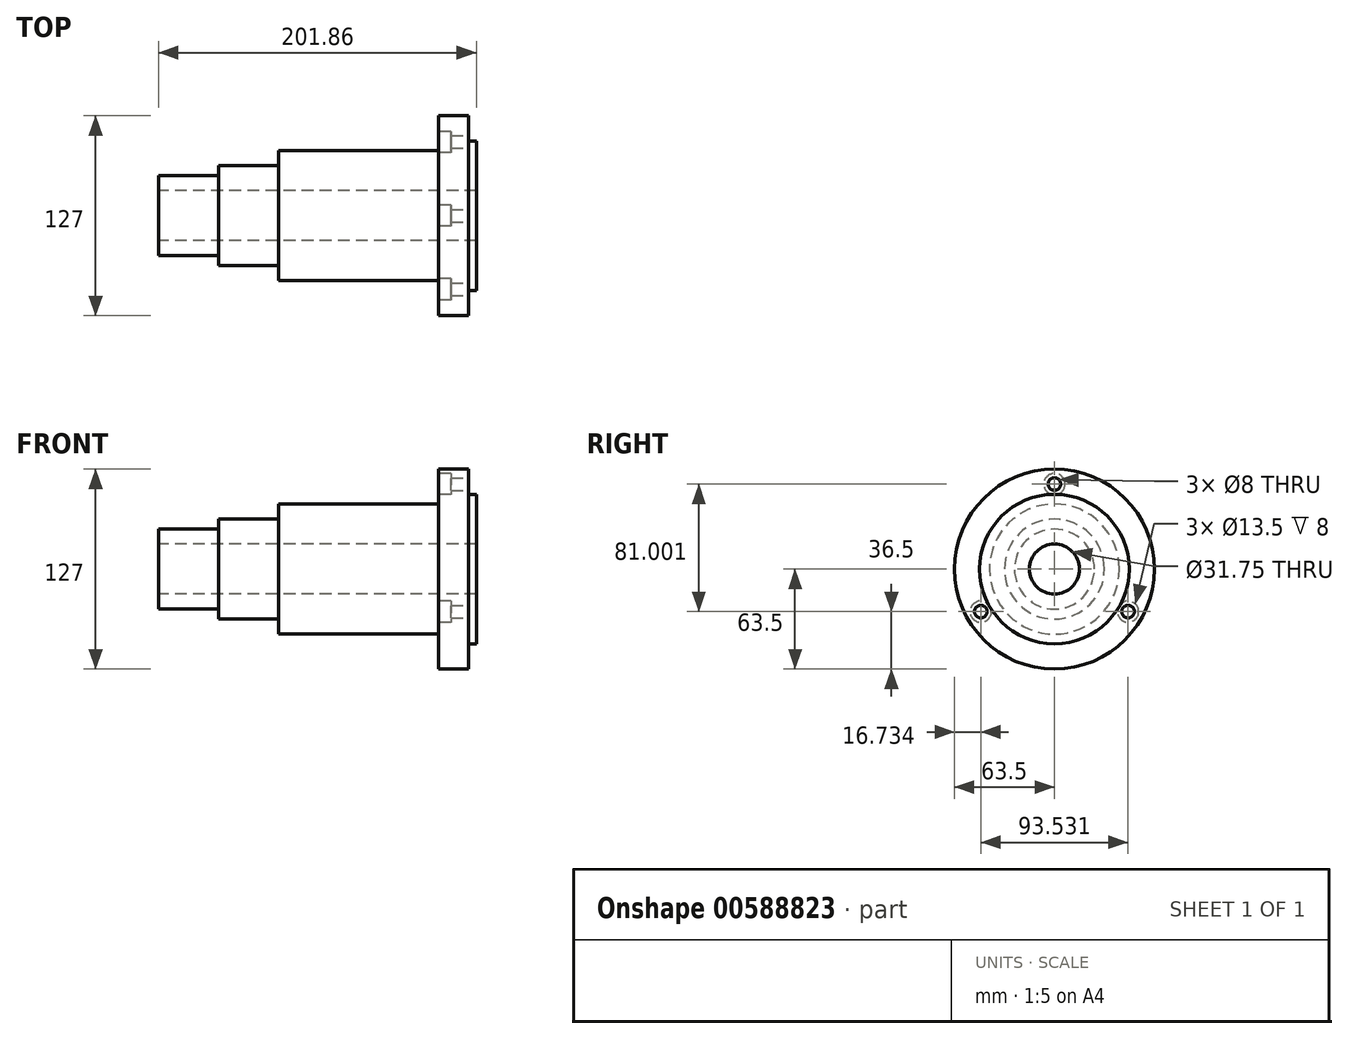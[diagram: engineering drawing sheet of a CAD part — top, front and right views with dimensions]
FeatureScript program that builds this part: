
annotation { "Feature Type Name" : "Feature", "Feature Type Description" : "" }
export const myFeature = defineFeature(function(context is Context, id is Id, definition is map)
    precondition{}
    {
        {
            var Q0;
            Q0=qCreatedBy(makeId("Front.planeOp"),FACE);
            var sketch = newSketch(context, id + "F0", { "sketchPlane" : qUnion([Q0])});
            skLineSegment(sketch, "E0", {"start": v(10.11, 15.88) * mm, "end": v(130.76, 15.88) * mm});
            skLineSegment(sketch, "E1", {"start": v(130.76, 47.5) * mm, "end": v(130.76, 63.5) * mm});
            skLineSegment(sketch, "E2", {"start": v(130.76, 63.5) * mm, "end": v(111.71, 63.5) * mm});
            skLineSegment(sketch, "E3", {"start": v(111.71, 63.5) * mm, "end": v(111.71, 41.28) * mm});
            skLineSegment(sketch, "E4", {"start": v(111.71, 41.28) * mm, "end": v(10.11, 41.28) * mm});
            skLineSegment(sketch, "E5", {"start": v(10.11, 41.28) * mm, "end": v(10.11, 31.75) * mm});
            skLineSegment(sketch, "E6.bottom", {"start": v(135.77, 47.5) * mm, "end": v(130.76, 47.5) * mm});
            skLineSegment(sketch, "E6.top", {"start": v(135.77, 15.88) * mm, "end": v(130.76, 15.88) * mm});
            skLineSegment(sketch, "E6.left", {"start": v(135.77, 47.5) * mm, "end": v(135.77, 15.88) * mm});
            skLineSegment(sketch, "E7.bottom", {"start": v(10.11, 15.88) * mm, "end": v(-47.18, 15.87) * mm});
            skLineSegment(sketch, "E7.top", {"start": v(10.11, 31.75) * mm, "end": v(-27.99, 31.75) * mm});
            skLineSegment(sketch, "E8.bottom", {"start": v(-47.18, 15.87) * mm, "end": v(-66.09, 15.87) * mm});
            skLineSegment(sketch, "E8.top", {"start": v(-27.99, 25.4) * mm, "end": v(-66.09, 25.4) * mm});
            skLineSegment(sketch, "E8.right", {"start": v(-66.09, 15.87) * mm, "end": v(-66.09, 25.4) * mm});
            skLineSegment(sketch, "E9", {"start": v(-27.99, 25.4) * mm, "end": v(-27.99, 31.75) * mm});
            skLineSegment(sketch, "E10", {"start": v(-72.6, 0) * mm, "end": v(74.38, 0) * mm});
            skSolve(sketch);
        }
        {
            var Q0;
            Q0=makeQuery(id+"F0.imprint","IMPRINT",FACE,{"disambiguationData":[TD([[makeQuery(id+"F0.imprint","IMPRINT",EDGE,{"derivedFrom":sQuery(id+"F0.wireOp",EDGE,"E0")}),1.0]])]});
            var Q1;
            Q1=sQuery(id+"F0.wireOp",EDGE,"E10");
            revolve(context, id + "F1", {"entities" : qUnion([Q0]), "axis" : qUnion([Q1]), "revolveType" : RevolveType.FULL});
        }
        {
            var Q0;
            Q0=makeQuery(id+"F1.opRevolve","SWEPT_FACE",FACE,{"disambiguationData":[OSD([sQuery(id+"F0.wireOp",EDGE,"E1")])]});
            var sketch = newSketch(context, id + "F2", { "sketchPlane" : qUnion([Q0])});
            skCircle(sketch, "E11", {"center": v(0, 0) * mm, "radius": 54 * mm, "construction": true});
            skCircle(sketch, "E12", {"center": v(0, 54) * mm, "radius": 4 * mm});
            skCircle(sketch, "E13.1.0", {"center": v(-46.77, -27) * mm, "radius": 4 * mm});
            skCircle(sketch, "E13.2.0", {"center": v(46.77, -27) * mm, "radius": 4 * mm});
            skSolve(sketch);
        }
        {
            var Q0;
            Q0=makeQuery(id+"F2.imprint","IMPRINT",FACE,{"disambiguationData":[TD([[makeQuery(id+"F2.imprint","IMPRINT",EDGE,{"derivedFrom":sQuery(id+"F2.wireOp",EDGE,"E12")}),1.0]])]});
            var Q1;
            Q1=makeQuery(id+"F2.imprint","IMPRINT",FACE,{"disambiguationData":[TD([[makeQuery(id+"F2.imprint","IMPRINT",EDGE,{"derivedFrom":sQuery(id+"F2.wireOp",EDGE,"E13.2.0")}),1.0]])]});
            var Q2;
            Q2=makeQuery(id+"F2.imprint","IMPRINT",FACE,{"disambiguationData":[TD([[makeQuery(id+"F2.imprint","IMPRINT",EDGE,{"derivedFrom":sQuery(id+"F2.wireOp",EDGE,"E13.1.0")}),1.0]])]});
            extrude(context, id + "F3", {"entities" : qUnion([Q0, Q1, Q2]), "operationType" : NewBodyOperationType.REMOVE, "oppositeDirection" : true, "depth" : 25.4 * mm, "offsetDistance" : 25.4 * mm});
        }
        {
            var Q0;
            Q0=makeQuery(id+"F1.opRevolve","SWEPT_FACE",FACE,{"disambiguationData":[OSD([sQuery(id+"F0.wireOp",EDGE,"E3")])]});
            var sketch = newSketch(context, id + "F4", { "sketchPlane" : qUnion([Q0])});
            skCircle(sketch, "E14", {"center": v(0, 54) * mm, "radius": 6.75 * mm});
            skCircle(sketch, "E15.1.0", {"center": v(-46.77, -27) * mm, "radius": 6.75 * mm});
            skCircle(sketch, "E15.2.0", {"center": v(46.77, -27) * mm, "radius": 6.75 * mm});
            skPoint(sketch, "E15.center", {"position": v(0, 0) * mm});
            skSolve(sketch);
        }
        {
            var Q0;
            Q0=makeQuery(id+"F4.imprint","IMPRINT",FACE,{"disambiguationData":[TD([[makeQuery(id+"F4.imprint","IMPRINT",EDGE,{"derivedFrom":sQuery(id+"F4.wireOp",EDGE,"E14")}),1.0]])]});
            var Q1;
            Q1=makeQuery(id+"F4.imprint","IMPRINT",FACE,{"disambiguationData":[TD([[makeQuery(id+"F4.imprint","IMPRINT",EDGE,{"derivedFrom":sQuery(id+"F4.wireOp",EDGE,"E15.2.0")}),1.0]])]});
            var Q2;
            Q2=makeQuery(id+"F4.imprint","IMPRINT",FACE,{"disambiguationData":[TD([[makeQuery(id+"F4.imprint","IMPRINT",EDGE,{"derivedFrom":sQuery(id+"F4.wireOp",EDGE,"E15.1.0")}),1.0]])]});
            extrude(context, id + "F5", {"entities" : qUnion([Q0, Q1, Q2]), "operationType" : NewBodyOperationType.REMOVE, "oppositeDirection" : true, "depth" : 8 * mm, "offsetDistance" : 25.4 * mm});
        }
    });
